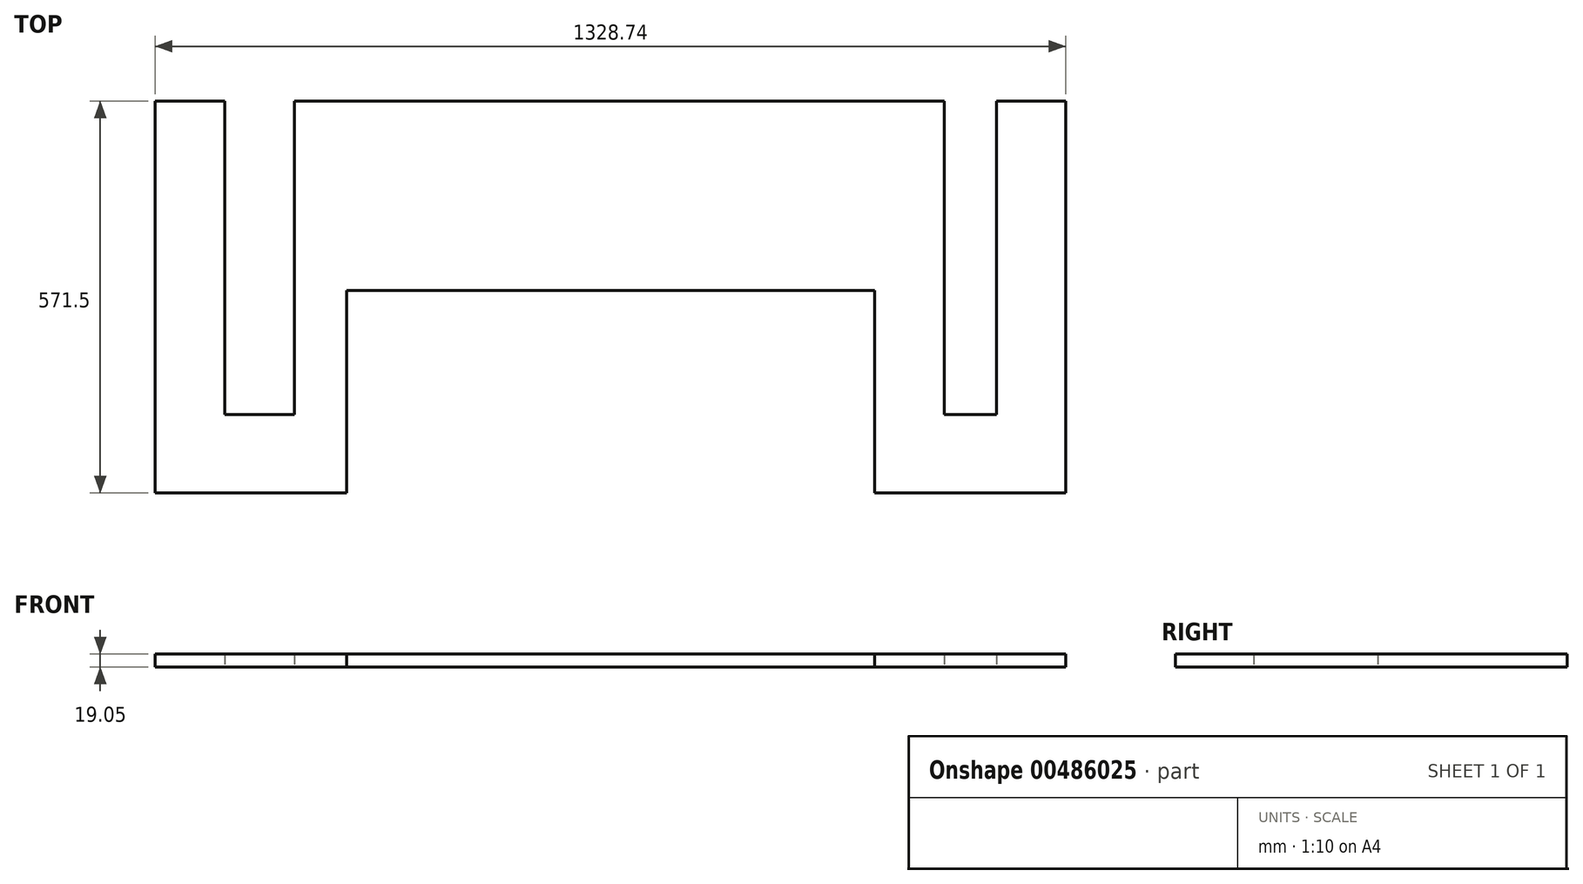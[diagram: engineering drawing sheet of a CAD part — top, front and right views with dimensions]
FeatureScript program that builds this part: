
annotation { "Feature Type Name" : "Feature", "Feature Type Description" : "" }
export const myFeature = defineFeature(function(context is Context, id is Id, definition is map)
    precondition{}
    {
        {
            var Q0;
            Q0=qCreatedBy(makeId("Top.planeOp"),FACE);
            var sketch = newSketch(context, id + "F0", { "sketchPlane" : qUnion([Q0])});
            skLineSegment(sketch, "E0", {"start": v(-126.27, 212.66) * mm, "end": v(-24.67, 212.66) * mm});
            skLineSegment(sketch, "E1", {"start": v(-24.67, 212.66) * mm, "end": v(-24.67, -244.54) * mm});
            skLineSegment(sketch, "E2", {"start": v(-126.27, 212.66) * mm, "end": v(-126.27, -358.84) * mm});
            skLineSegment(sketch, "E3", {"start": v(-126.27, -358.84) * mm, "end": v(153.13, -358.84) * mm});
            skLineSegment(sketch, "E4", {"start": v(153.13, -358.84) * mm, "end": v(153.13, -63.65) * mm});
            skLineSegment(sketch, "E5", {"start": v(153.13, -63.65) * mm, "end": v(923.07, -63.65) * mm});
            skLineSegment(sketch, "E6", {"start": v(923.07, -63.65) * mm, "end": v(923.07, -358.84) * mm});
            skLineSegment(sketch, "E7", {"start": v(923.07, -358.84) * mm, "end": v(1202.47, -358.84) * mm});
            skLineSegment(sketch, "E8", {"start": v(1202.47, -358.84) * mm, "end": v(1202.47, 212.66) * mm});
            skLineSegment(sketch, "E9", {"start": v(1202.47, 212.66) * mm, "end": v(1100.87, 212.66) * mm});
            skLineSegment(sketch, "E10", {"start": v(1100.87, 212.66) * mm, "end": v(1100.87, -244.54) * mm});
            skLineSegment(sketch, "E11", {"start": v(1100.87, -244.54) * mm, "end": v(1024.67, -244.54) * mm});
            skLineSegment(sketch, "E12", {"start": v(1024.67, -244.54) * mm, "end": v(1024.67, 212.66) * mm});
            skLineSegment(sketch, "E13", {"start": v(-24.67, -244.54) * mm, "end": v(76.93, -244.54) * mm});
            skLineSegment(sketch, "E14", {"start": v(76.93, -244.54) * mm, "end": v(76.93, 212.66) * mm});
            skLineSegment(sketch, "E15", {"start": v(76.93, 212.66) * mm, "end": v(1024.67, 212.66) * mm});
            skSolve(sketch);
        }
        {
            var Q0;
            Q0 = qSketchRegion(id + "F0", true);
            extrude(context, id + "F1", {"entities" : qUnion([Q0]), "depth" : 19.05 * mm, "offsetDistance" : 25.4 * mm});
        }
    });
